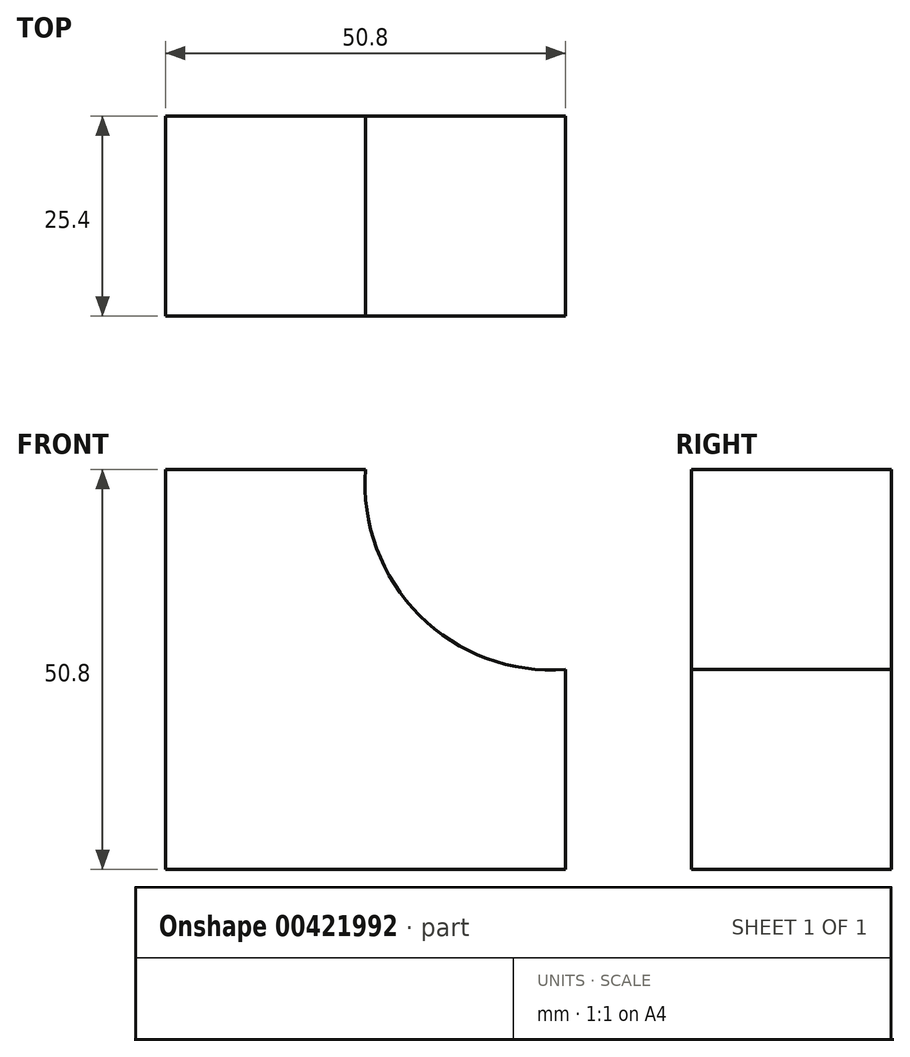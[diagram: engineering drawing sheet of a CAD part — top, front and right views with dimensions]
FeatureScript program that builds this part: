
annotation { "Feature Type Name" : "Feature", "Feature Type Description" : "" }
export const myFeature = defineFeature(function(context is Context, id is Id, definition is map)
    precondition{}
    {
        {
            var Q0;
            Q0=qCreatedBy(makeId("Front.planeOp"),FACE);
            var sketch = newSketch(context, id + "F0", { "sketchPlane" : qUnion([Q0])});
            skLineSegment(sketch, "E0", {"start": v(0, 0) * mm, "end": v(-50.8, 0) * mm});
            skLineSegment(sketch, "E1", {"start": v(-50.8, 0) * mm, "end": v(-50.8, 50.8) * mm});
            skLineSegment(sketch, "E2", {"start": v(-50.8, 50.8) * mm, "end": v(-25.4, 50.8) * mm});
            skLineSegment(sketch, "E3", {"start": v(0, 0) * mm, "end": v(0, 25.4) * mm});
            skArc(sketch, "E4", {"start": v(-25.4, 50.8) * mm, "mid": v(-18.54, 32.26) * mm, "end": v(0, 25.4) * mm});
            skSolve(sketch);
        }
        {
            var Q0;
            Q0 = qSketchRegion(id + "F0", true);
            extrude(context, id + "F1", {"entities" : qUnion([Q0]), "depth" : 25.4 * mm});
        }
    });
